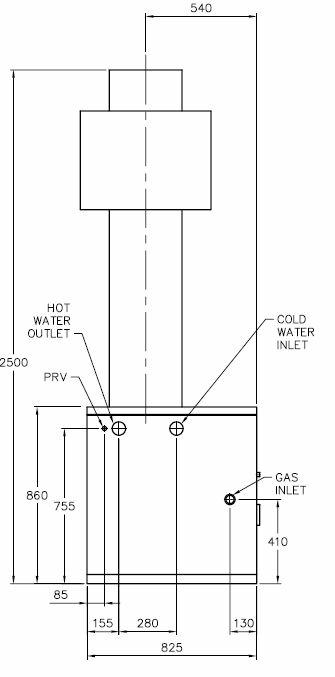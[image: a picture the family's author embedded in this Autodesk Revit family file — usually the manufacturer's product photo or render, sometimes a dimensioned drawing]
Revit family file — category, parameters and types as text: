
# Revit family: DC_Rheem_PLM_Raypak_B0972HWT
name_source: partatom
category: Plumbing Fixtures
revit_build: Autodesk Revit 2017 (Build: 20160225_1515(x64)
units: mm (PartAtom-declared; Revit-internal decimal feet)

## family parameters
Cut with Voids When Loaded = No
Host = Face
Part Type = Normal
Room Calculation Point = No
Round Connector Dimension = Use Radius
Shared = No

## types (4) — shared parameters
BoxHeight_ANZRS = 860 mm  [stored 2.82152 ft]
ColdWaterPipeDiameter_ANZRS = 65 mm  [stored 0.213255 ft]
ColdWaterPipeRadius_ANZRS = 33 mm
ConnectorHeight_ANZRS = 755 mm
Description = Raypak - Gas Water Heater- Outdoor - 976 MJ/h  Natural gas, modulating gas control
GasInletHeight_ANZRS = 410 mm  [stored 1.34514 ft]
Height_ANZRS = 2500 mm  [stored 8.2021 ft]
HotWaterPipeDiameter_ANZRS = 65 mm  [stored 0.213255 ft]
HotWaterPipeRadius_ANZRS = 33 mm
Length_ANZRS = 1330 mm
Manufacturer = Raypak
Materials_ANZRS = Raypak - Grey Powder Coated Steel
PRVDiameter_ANZRS = 15 mm  [stored 0.0492126 ft]
PRVRadius_ANZRS = 8 mm  [stored 0.0262467 ft]
URL = http://www.rheem.com.au
Width_ANZRS = 825 mm  [stored 2.70669 ft]
zero-valued in all types: Default Elevation

## per-type parameters (varying)
| type | GasInletDiameter_ANZRS | GasInletRadius_ANZRS | Model | Type Comments |
| Raypak - Gas Water Heater- Outdoor - 976 MJ/h  Natural gas, modulating gas control | 40 mm  [stored 0.131234 ft] | 20 mm  [stored 0.0656168 ft] | B0976NCM/HWT | Recovery 3784L/h @ 50oC rise |
| Raypak - Gas Water Heater- Outdoor - 976 MJ/h  Natural gas, On/Off gas control | 40 mm  [stored 0.131234 ft] | 20 mm  [stored 0.0656168 ft] | B0976NCO/HWT | Recovery 3784L/h @ 50oC rise |
| Raypak - Gas Water Heater- Outdoor - 933 MJ/h  Propane gas, modulating gas control | 20 mm  [stored 0.0656168 ft] | 10 mm  [stored 0.0328084 ft] | B0976PCM/HWT | Recovery 3526L/h @ 50oC rise |
| Raypak - Gas Water Heater- Outdoor - 933 MJ/h  Propane gas, On/Off gas control | 32 mm  [stored 0.104987 ft] | 16 mm  [stored 0.0524934 ft] | B0976PCO/HWT | Recovery 3526L/h @ 50oC rise |

note: [stored X ft] marks values corroborated as IEEE doubles in the binary element streams (Revit-internal decimal feet)

## geometry (parser evidence)
native form markers: Blend x2, Sweep x2
no freeform markers — native parametric forms only
